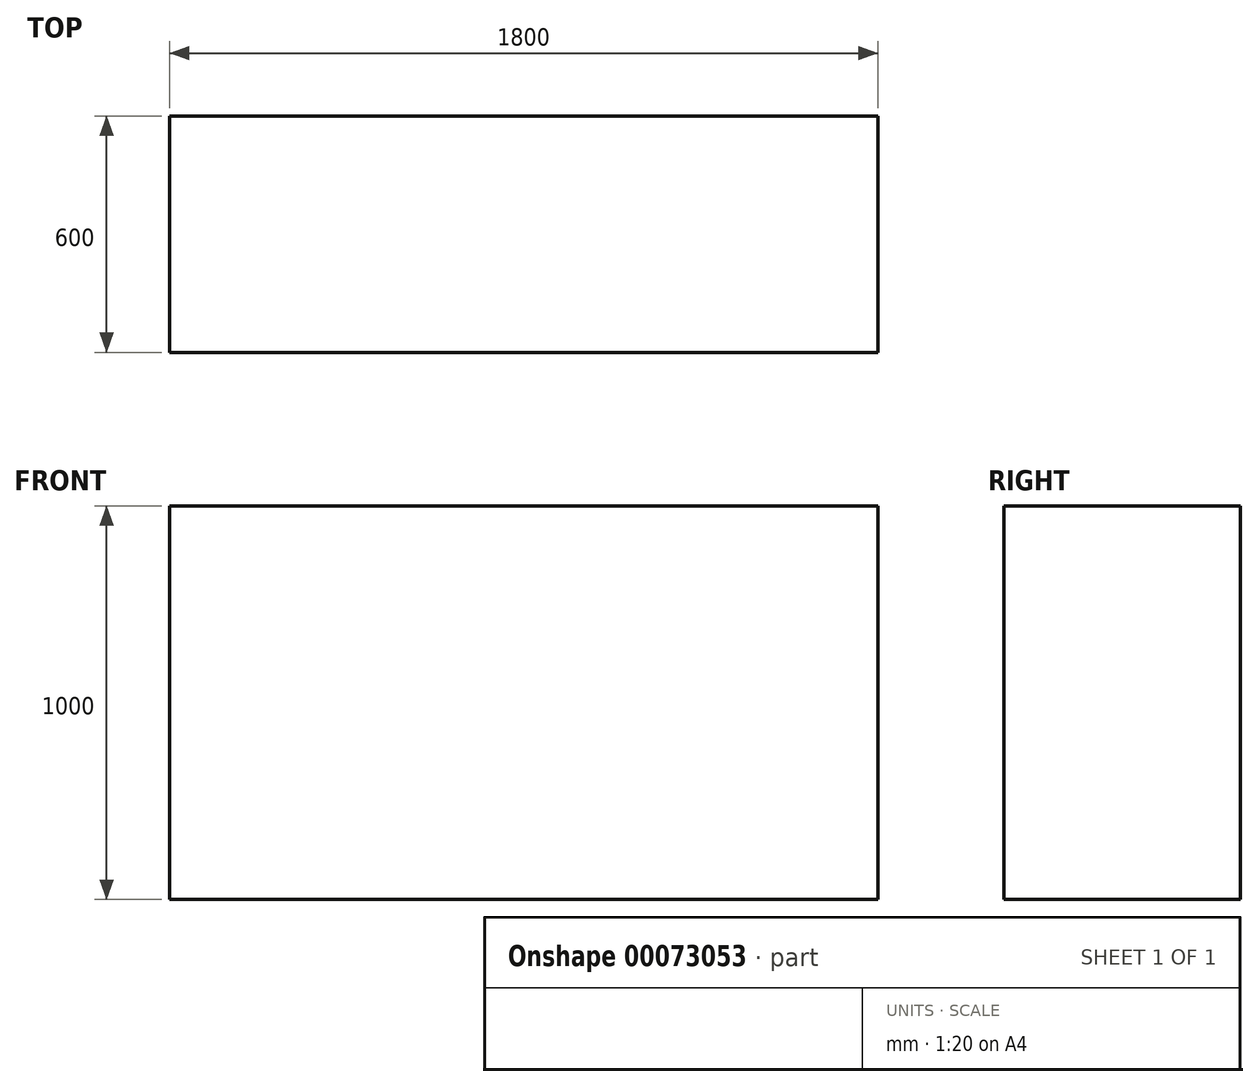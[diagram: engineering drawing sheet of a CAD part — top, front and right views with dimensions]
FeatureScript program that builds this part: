
annotation { "Feature Type Name" : "Feature", "Feature Type Description" : "" }
export const myFeature = defineFeature(function(context is Context, id is Id, definition is map)
    precondition{}
    {
        {
            var Q0;
            Q0=qCreatedBy(makeId("Top.planeOp"),FACE);
            var sketch = newSketch(context, id + "F0", { "sketchPlane" : qUnion([Q0])});
            skLineSegment(sketch, "E0.bottom", {"start": v(900, -300) * mm, "end": v(-900, -300) * mm});
            skLineSegment(sketch, "E0.top", {"start": v(900, 300) * mm, "end": v(-900, 300) * mm});
            skLineSegment(sketch, "E0.left", {"start": v(900, -300) * mm, "end": v(900, 300) * mm});
            skLineSegment(sketch, "E0.right", {"start": v(-900, -300) * mm, "end": v(-900, 300) * mm});
            skPoint(sketch, "E0.middle", {"position": v(0, 0) * mm});
            skSolve(sketch);
        }
        {
            var Q0;
            Q0=makeQuery(id+"F0.imprint","IMPRINT",FACE,{"disambiguationData":[TD([[makeQuery(id+"F0.imprint","IMPRINT",EDGE,{"derivedFrom":sQuery(id+"F0.wireOp",EDGE,"E0.bottom")}),-1.0]])]});
            extrude(context, id + "F1", {"entities" : qUnion([Q0]), "depth" : 1000 * mm});
        }
    });
